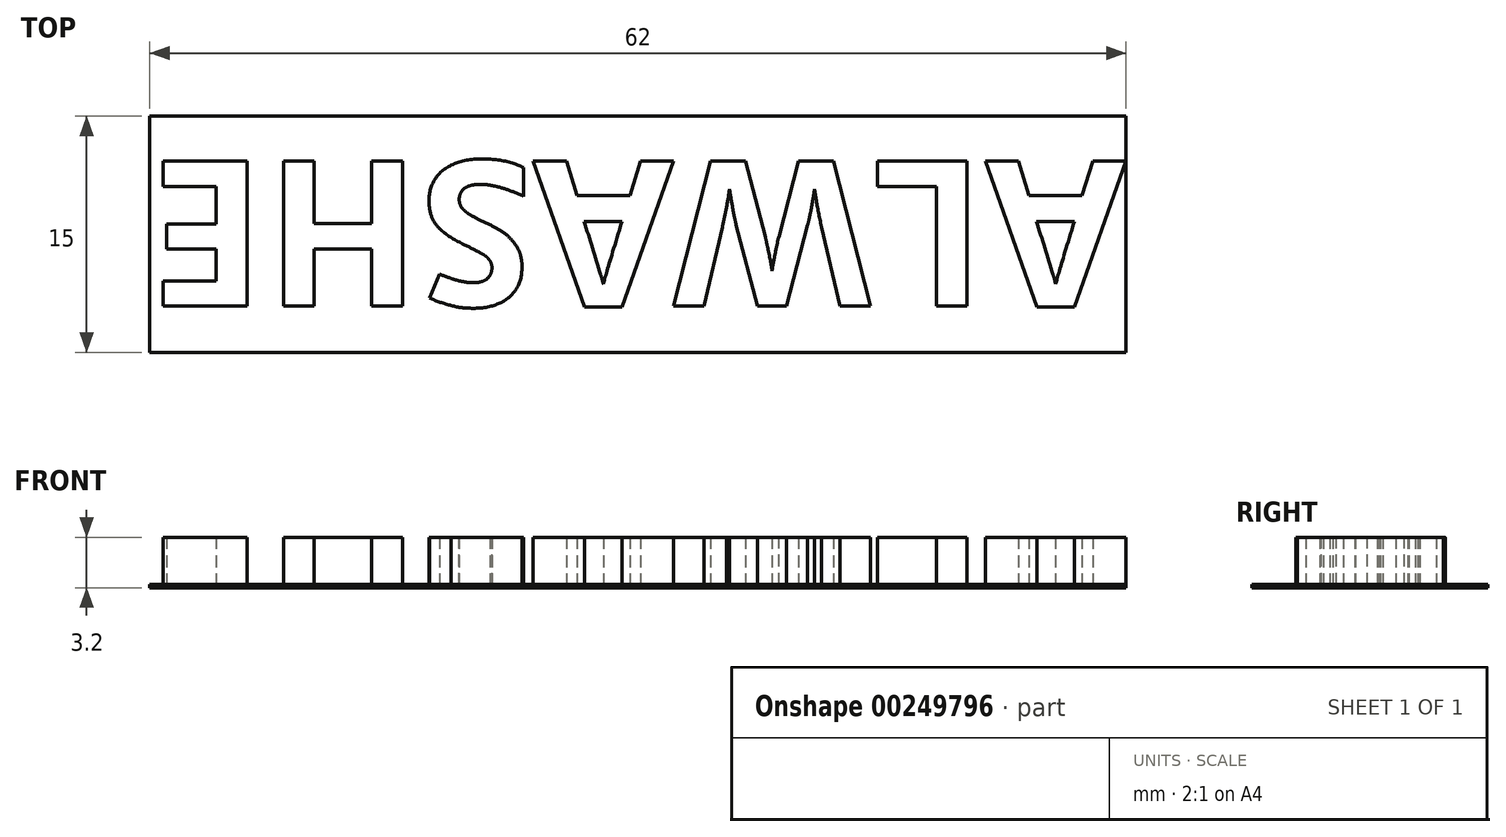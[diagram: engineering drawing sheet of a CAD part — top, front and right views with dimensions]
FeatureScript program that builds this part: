
annotation { "Feature Type Name" : "Feature", "Feature Type Description" : "" }
export const myFeature = defineFeature(function(context is Context, id is Id, definition is map)
    precondition{}
    {
        {
            var Q0;
            Q0=qCreatedBy(makeId("Top.planeOp"),FACE);
            var sketch = newSketch(context, id + "F0", { "sketchPlane" : qUnion([Q0])});
            skLineSegment(sketch, "E0.bottom", {"start": v(31, -7.5) * mm, "end": v(-31, -7.5) * mm});
            skLineSegment(sketch, "E0.top", {"start": v(31, 7.5) * mm, "end": v(-31, 7.5) * mm});
            skLineSegment(sketch, "E0.left", {"start": v(31, -7.5) * mm, "end": v(31, 7.5) * mm});
            skLineSegment(sketch, "E0.right", {"start": v(-31, -7.5) * mm, "end": v(-31, 7.5) * mm});
            skPoint(sketch, "E0.middle", {"position": v(0, 0) * mm});
            skSolve(sketch);
        }
        {
            var Q0;
            Q0=makeQuery(id+"F0.imprint","IMPRINT",FACE,{"disambiguationData":[TD([[makeQuery(id+"F0.imprint","IMPRINT",EDGE,{"derivedFrom":sQuery(id+"F0.wireOp",EDGE,"E0.bottom")}),-1.0]])]});
            extrude(context, id + "F1", {"entities" : qUnion([Q0]), "depth" : 0.2 * mm});
        }
        {
            var Q0;
            Q0=makeQuery(id+"F1.opExtrude","CAP_FACE",FACE,{"disambiguationData":[OSD([sQuery(id+"F0.wireOp",EDGE,"E0.bottom"),sQuery(id+"F0.wireOp",EDGE,"E0.top"),sQuery(id+"F0.wireOp",EDGE,"E0.left"),sQuery(id+"F0.wireOp",EDGE,"E0.right")])],"isStart":false});
            var sketch = newSketch(context, id + "F2", { "sketchPlane" : qUnion([Q0])});
            skText(sketch, "E1", { "text": "ALWASHE", "fontName": "OpenSans-Bold.ttf"});
            skLineSegment(sketch, "E2", {"start": v(31, -6.78) * mm, "end": v(-31, -6.78) * mm, "construction": true});
            const initialGuessF2  = {"E1": [0.031, 0.00466, -1, 0, 0.00931]};
            skSetInitialGuess(sketch, initialGuessF2);
            skSolve(sketch);
        }
        {
            var Q0;
            Q0=makeQuery(id+"F2.imprint","IMPRINT",FACE,{"disambiguationData":[TD([[makeQuery(id+"F2.imprint","IMPRINT",EDGE,{"derivedFrom":sQuery(id+"F2.wireOp",EDGE,"E1.sketch_text.stroke-0")}),-1.0]])]});
            var Q1;
            Q1=makeQuery(id+"F2.imprint","IMPRINT",FACE,{"disambiguationData":[TD([[makeQuery(id+"F2.imprint","IMPRINT",EDGE,{"derivedFrom":sQuery(id+"F2.wireOp",EDGE,"E1.sketch_text.stroke-12")}),-1.0]])]});
            var Q2;
            Q2=makeQuery(id+"F2.imprint","IMPRINT",FACE,{"disambiguationData":[TD([[makeQuery(id+"F2.imprint","IMPRINT",EDGE,{"derivedFrom":sQuery(id+"F2.wireOp",EDGE,"E1.sketch_text.stroke-18")}),-1.0]])]});
            var Q3;
            Q3=makeQuery(id+"F2.imprint","IMPRINT",FACE,{"disambiguationData":[TD([[makeQuery(id+"F2.imprint","IMPRINT",EDGE,{"derivedFrom":sQuery(id+"F2.wireOp",EDGE,"E1.sketch_text.stroke-42")}),-1.0]])]});
            var Q4;
            Q4=makeQuery(id+"F2.imprint","IMPRINT",FACE,{"disambiguationData":[TD([[makeQuery(id+"F2.imprint","IMPRINT",EDGE,{"derivedFrom":sQuery(id+"F2.wireOp",EDGE,"E1.sketch_text.stroke-54")}),-1.0]])]});
            var Q5;
            Q5=makeQuery(id+"F2.imprint","IMPRINT",FACE,{"disambiguationData":[TD([[makeQuery(id+"F2.imprint","IMPRINT",EDGE,{"derivedFrom":sQuery(id+"F2.wireOp",EDGE,"E1.sketch_text.stroke-82")}),-1.0]])]});
            var Q6;
            Q6=makeQuery(id+"F2.imprint","IMPRINT",FACE,{"disambiguationData":[TD([[makeQuery(id+"F2.imprint","IMPRINT",EDGE,{"derivedFrom":sQuery(id+"F2.wireOp",EDGE,"E1.sketch_text.stroke-94")}),-1.0]])]});
            extrude(context, id + "F3", {"entities" : qUnion([Q0, Q1, Q2, Q3, Q4, Q5, Q6]), "operationType" : NewBodyOperationType.ADD, "depth" : 3 * mm});
        }
    });
